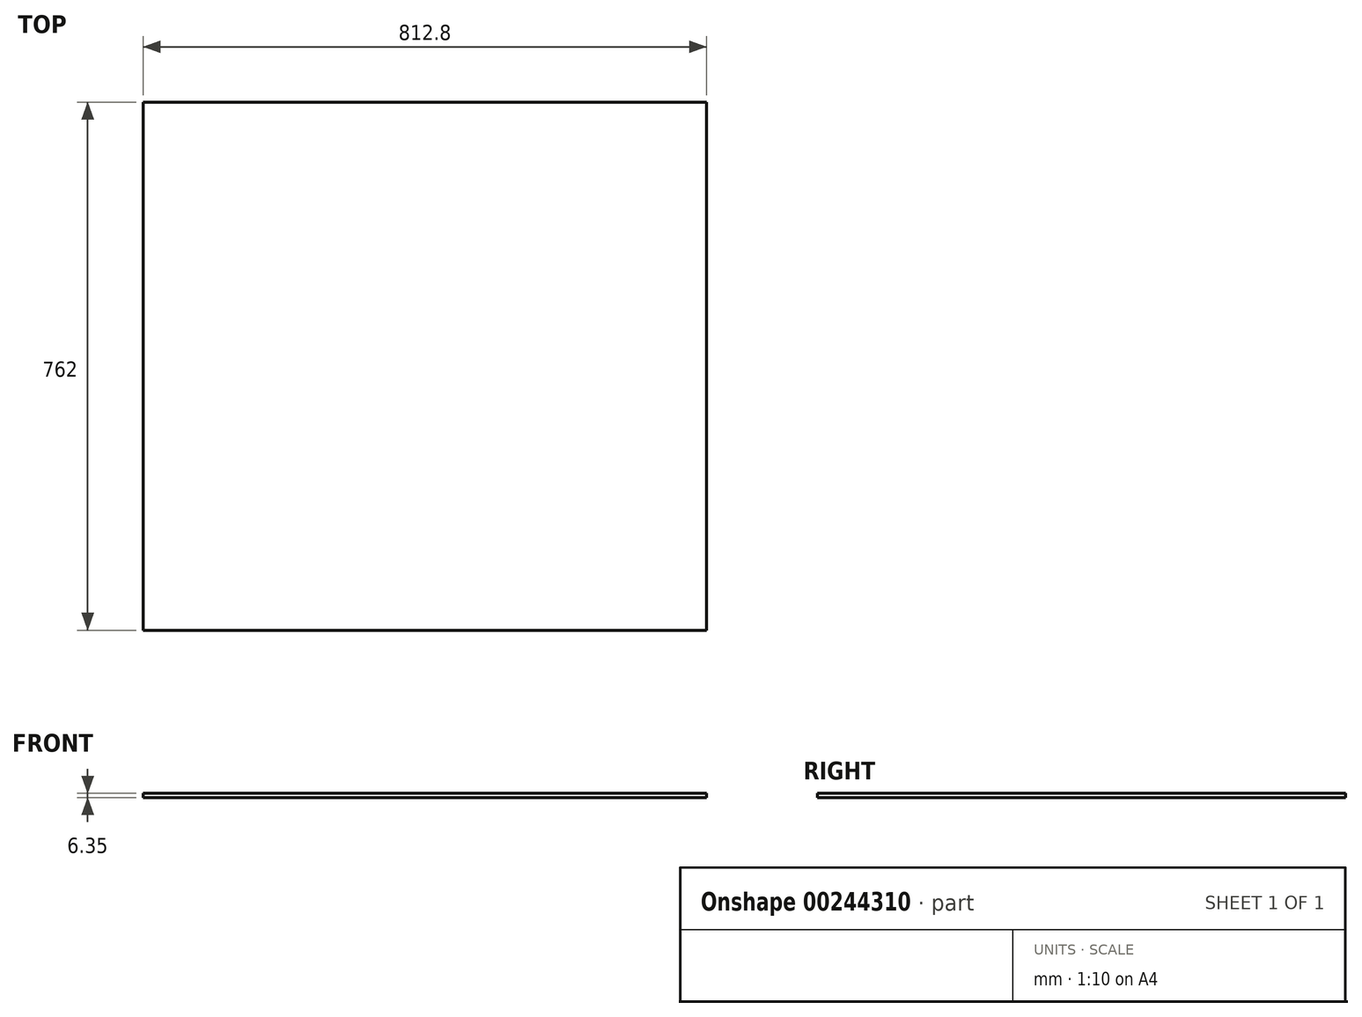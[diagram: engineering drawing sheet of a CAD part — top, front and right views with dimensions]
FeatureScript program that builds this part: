
annotation { "Feature Type Name" : "Feature", "Feature Type Description" : "" }
export const myFeature = defineFeature(function(context is Context, id is Id, definition is map)
    precondition{}
    {
        {
            var Q0;
            Q0=qCreatedBy(makeId("Top.planeOp"),FACE);
            var sketch = newSketch(context, id + "F0", { "sketchPlane" : qUnion([Q0])});
            skLineSegment(sketch, "E0.bottom", {"start": v(-443.08, 297.1) * mm, "end": v(369.72, 297.1) * mm});
            skLineSegment(sketch, "E0.top", {"start": v(-443.08, -464.9) * mm, "end": v(369.72, -464.9) * mm});
            skLineSegment(sketch, "E0.left", {"start": v(-443.08, 297.1) * mm, "end": v(-443.08, -464.9) * mm});
            skLineSegment(sketch, "E0.right", {"start": v(369.72, 297.1) * mm, "end": v(369.72, -464.9) * mm});
            skSolve(sketch);
        }
        {
            var Q0;
            Q0 = qSketchRegion(id + "F0", true);
            extrude(context, id + "F1", {"entities" : qUnion([Q0]), "depth" : 6.35 * mm});
        }
    });
